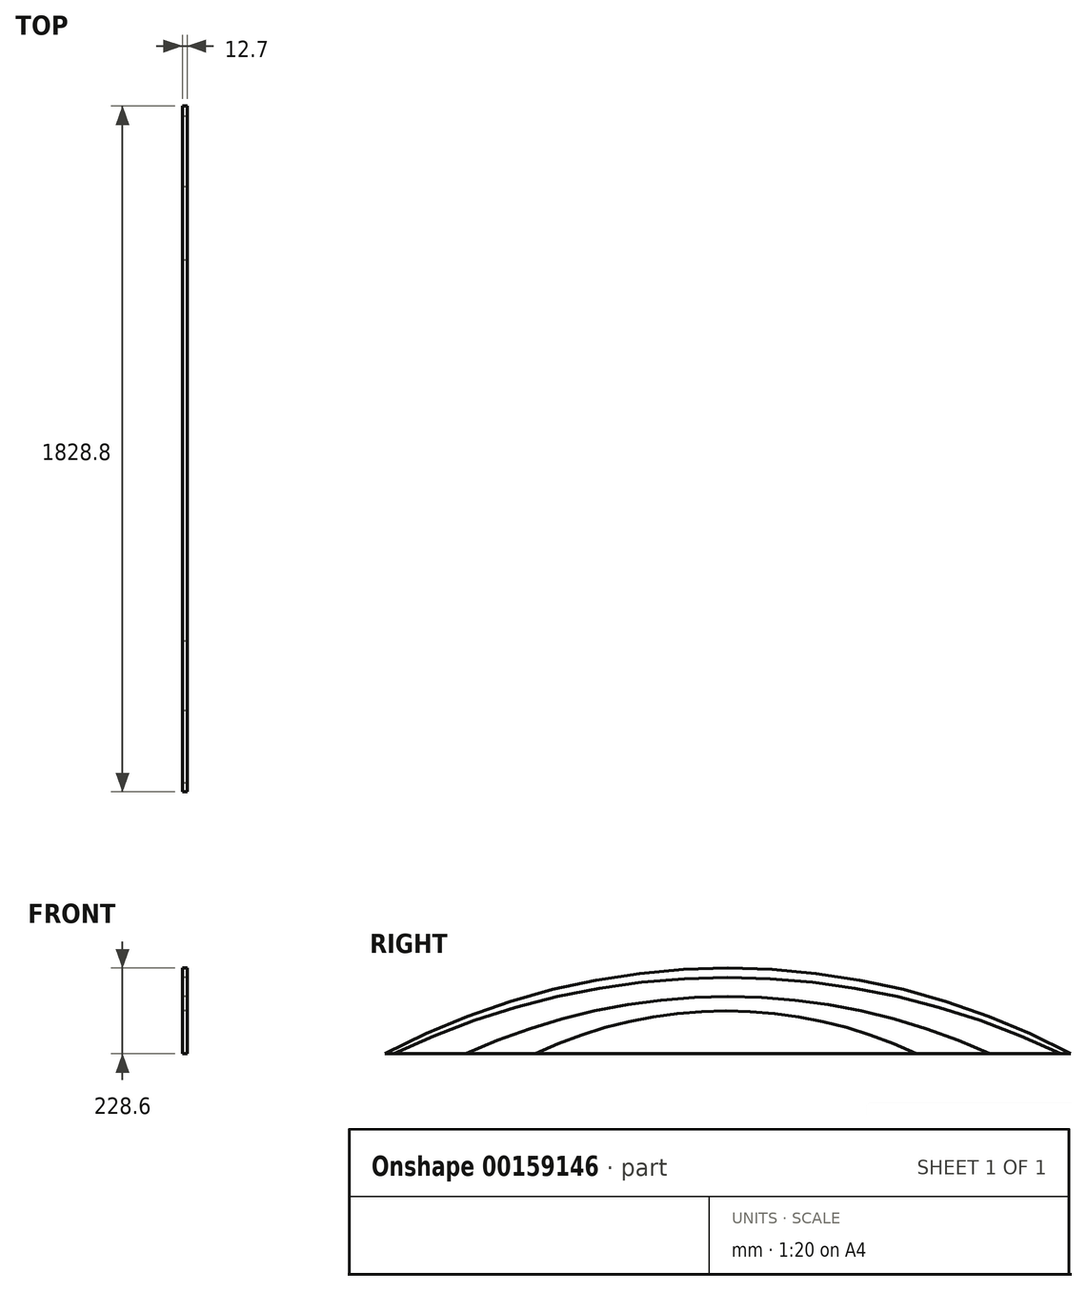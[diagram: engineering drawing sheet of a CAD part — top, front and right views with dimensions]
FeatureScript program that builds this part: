
annotation { "Feature Type Name" : "Feature", "Feature Type Description" : "" }
export const myFeature = defineFeature(function(context is Context, id is Id, definition is map)
    precondition{}
    {
        {
            var Q0;
            Q0=qCreatedBy(makeId("Right.planeOp"),FACE);
            var sketch = newSketch(context, id + "F0", { "sketchPlane" : qUnion([Q0])});
            skLineSegment(sketch, "E0", {"start": v(-912.44, 0) * mm, "end": v(916.36, 0) * mm});
            skArc(sketch, "E1", {"start": v(916.36, 0) * mm, "mid": v(1.96, 228.6) * mm, "end": v(-912.44, 0) * mm});
            skSolve(sketch);
        }
        {
            var Q0;
            Q0=makeQuery(id+"F0.imprint","IMPRINT",FACE,{"disambiguationData":[TD([[makeQuery(id+"F0.imprint","IMPRINT",EDGE,{"derivedFrom":sQuery(id+"F0.wireOp",EDGE,"E0")}),1.0]])]});
            extrude(context, id + "F1", {"entities" : qUnion([Q0]), "depth" : 12.7 * mm, "symmetric" : true});
        }
        {
            var Q0;
            Q0=qCreatedBy(makeId("Right.planeOp"),FACE);
            var sketch = newSketch(context, id + "F2", { "sketchPlane" : qUnion([Q0])});
            skLineSegment(sketch, "E2", {"start": v(-888.79, 0) * mm, "end": v(889.21, 0) * mm});
            skArc(sketch, "E3", {"start": v(889.21, 0) * mm, "mid": v(0.21, 203.2) * mm, "end": v(-888.79, 0) * mm});
            skSolve(sketch);
        }
        {
            var Q0;
            Q0 = qSketchRegion(id + "F2", true);
            extrude(context, id + "F3", {"entities" : qUnion([Q0]), "depth" : 12.7 * mm, "symmetric" : true});
        }
        {
            var Q0;
            Q0=qCreatedBy(makeId("Right.planeOp"),FACE);
            var sketch = newSketch(context, id + "F4", { "sketchPlane" : qUnion([Q0])});
            skLineSegment(sketch, "E4", {"start": v(-696.24, 0) * mm, "end": v(700.76, 0) * mm});
            skArc(sketch, "E5", {"start": v(700.76, 0) * mm, "mid": v(2.26, 152.4) * mm, "end": v(-696.24, 0) * mm});
            skSolve(sketch);
        }
        {
            var Q0;
            Q0 = qSketchRegion(id + "F4", true);
            extrude(context, id + "F5", {"entities" : qUnion([Q0]), "depth" : 12.7 * mm, "symmetric" : true});
        }
        {
            var Q0;
            Q0=qCreatedBy(makeId("Right.planeOp"),FACE);
            var sketch = newSketch(context, id + "F6", { "sketchPlane" : qUnion([Q0])});
            skLineSegment(sketch, "E6", {"start": v(-511.24, 0) * mm, "end": v(504.76, 0) * mm});
            skArc(sketch, "E7", {"start": v(504.76, 0) * mm, "mid": v(-3.24, 114.3) * mm, "end": v(-511.24, 0) * mm});
            skSolve(sketch);
        }
        {
            var Q0;
            Q0 = qSketchRegion(id + "F6", true);
            extrude(context, id + "F7", {"entities" : qUnion([Q0]), "depth" : 12.7 * mm, "symmetric" : true});
        }
    });
